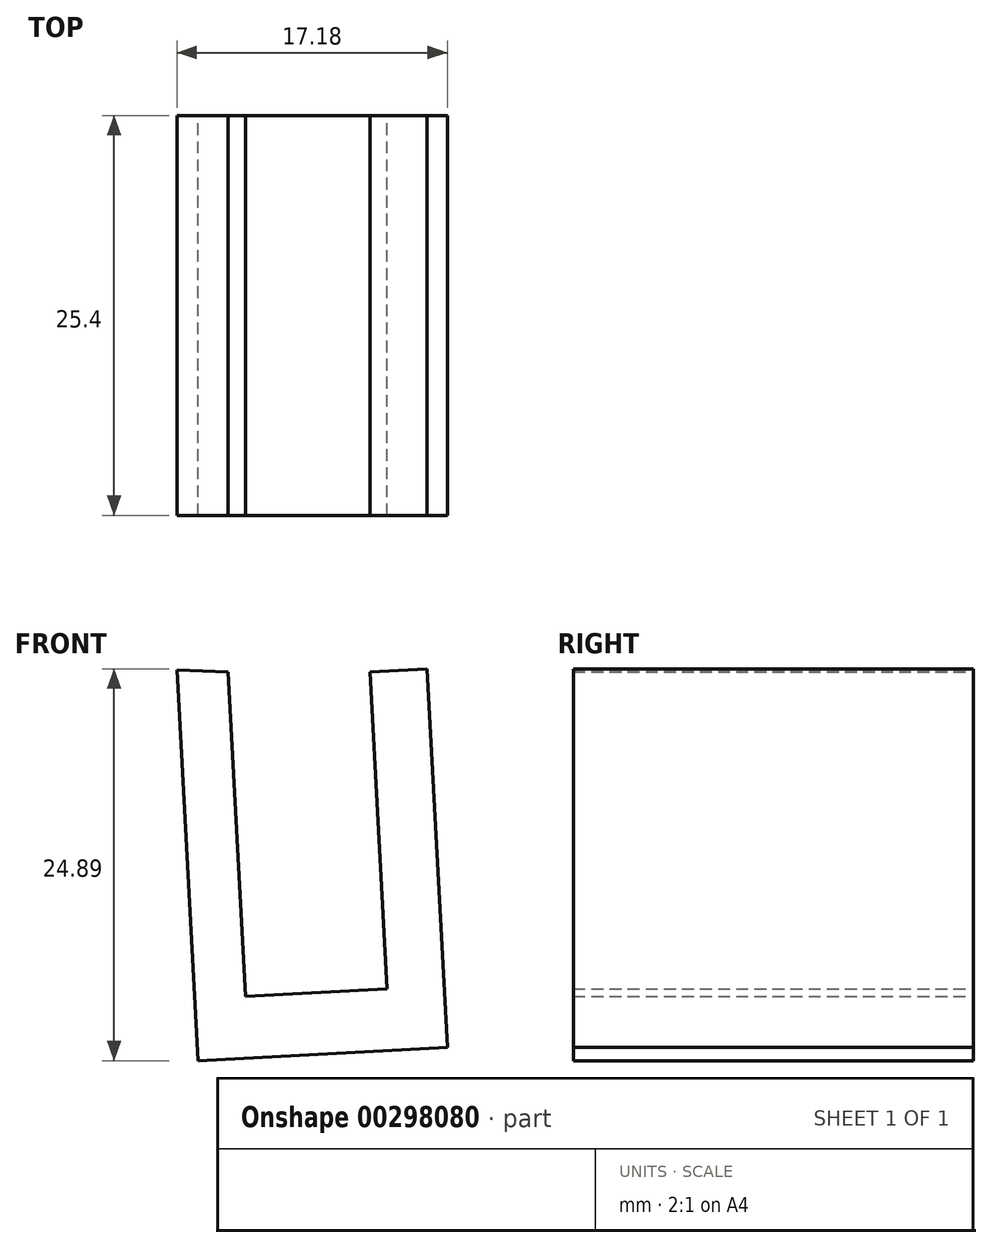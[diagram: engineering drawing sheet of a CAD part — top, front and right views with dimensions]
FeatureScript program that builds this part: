
annotation { "Feature Type Name" : "Feature", "Feature Type Description" : "" }
export const myFeature = defineFeature(function(context is Context, id is Id, definition is map)
    precondition{}
    {
        {
            var Q0;
            Q0=qCreatedBy(makeId("Front.planeOp"),FACE);
            var sketch = newSketch(context, id + "F0", { "sketchPlane" : qUnion([Q0])});
            skLineSegment(sketch, "E0", {"start": v(-66.45, 47.93) * mm, "end": v(-65.12, 23.1) * mm});
            skLineSegment(sketch, "E1", {"start": v(-65.12, 23.1) * mm, "end": v(-49.27, 23.96) * mm});
            skLineSegment(sketch, "E2", {"start": v(-49.27, 23.96) * mm, "end": v(-50.57, 48) * mm});
            skLineSegment(sketch, "E3", {"start": v(-50.57, 48) * mm, "end": v(-54.18, 47.8) * mm});
            skLineSegment(sketch, "E4", {"start": v(-54.18, 47.8) * mm, "end": v(-53.1, 27.67) * mm});
            skLineSegment(sketch, "E5", {"start": v(-53.1, 27.67) * mm, "end": v(-62.08, 27.18) * mm});
            skLineSegment(sketch, "E6", {"start": v(-62.08, 27.18) * mm, "end": v(-63.2, 47.8) * mm});
            skLineSegment(sketch, "E7", {"start": v(-63.2, 47.8) * mm, "end": v(-66.45, 47.93) * mm});
            skSolve(sketch);
        }
        {
            var Q0;
            Q0 = qSketchRegion(id + "F0", true);
            extrude(context, id + "F1", {"entities" : qUnion([Q0]), "depth" : 25.4 * mm});
        }
    });
